# Revit family: 2-5140-24 Zenith
name_source: partatom
category: Lighting Fixtures
revit_build: Autodesk Revit LT 2014 (Build: 20130308_1515(x64)
units: mm (PartAtom-declared; Revit-internal decimal feet)

## types (1)
- 2-5140-24 Zenith
    ADA Compliant = No
    Apparent Load = 18 VA
    Ballast Manufacturer = Antron
    Color Filter = 16777215
    Default Elevation = 4' - 0"
    Description = 24" Vanity - 1xT-5 Linear fluorescent
    Diffuser = Acrylic- Matte White
    Dimming Lamp Color Temperature Shift = <None>
    Emit Shape Visible in Rendering = No
    Emit from Rectangle Length = 4' - 0"
    Emit from Rectangle Width = 2' - 0"
    Fixture Height = 0' - 3 1/16"
    Fixture Length = 2' - 0 3/32"
    Input Power (Watts) = 18 W
    Input Voltage (VAC) = 120.0
    Junction Box = 2"x3" Juntion Box
    Lamp = 1x14W T-5 Fp14/841/ECO Linear Fluorescent
    Lamp Manufacturer = Sylvania
    Manufacturer = Oxygen Lighting
    Metal Finish = Satin Nickel
    Model = 2-5140-24
    Photometric Web File = 2-5140-24 Zenith 24 ITL77181.IES
    Power Factor = 0.99
    Product Documentation Link = http://oxygenlighting.com.s3.amazonaws.com
    Tilt Angle = -90.00°
    Type Comments = Lighting - Fluorescent
    URL = http://www.oxygenlighting.com

## geometry (parser evidence)
native form markers: Sweep x1
no freeform markers — native parametric forms only
